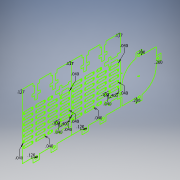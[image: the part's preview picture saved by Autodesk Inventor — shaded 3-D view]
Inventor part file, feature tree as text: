
AUTODESK INVENTOR PART (.ipt)
format: ipt  version: 2016 (Build 200138000, 138)  size: 292,352 bytes
history: native  units: in
note: dims shown in document units (in); Inventor stores cm internally (conversion verified against a paired STEP export)
features: sketch x1
ambient origin geometry x8: Origin, YZ Plane, XZ Plane, XY Plane, X Axis, Y Axis, Z Axis, Center Point
feature tree (1):
  sketch  "Sketch1"  dims[d30=0.12in d36=0.117in d68=0.117in d73=0.2in d74=0.2in d75=0.2in d80=0.4in d81=0.1in d90=0.04in d91=0.04in d92=0.04in d93=0.04in d94=0.04in d95=0.12in d96=0.117in d97=0.117in d98=0.4in d99=0.1in d100=0.04in d101=0.04in d102=0.04in d103=0.04in d104=0.04in]
